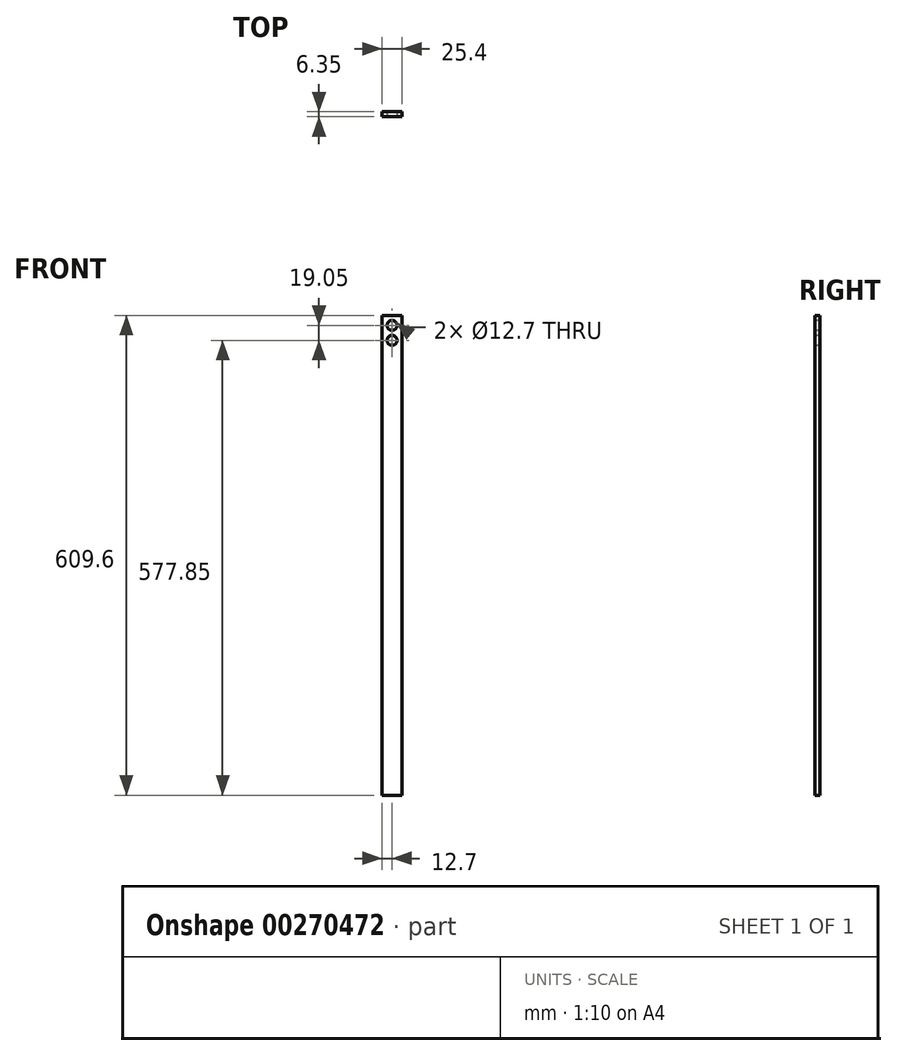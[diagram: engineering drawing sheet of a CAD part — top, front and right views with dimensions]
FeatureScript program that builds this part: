
annotation { "Feature Type Name" : "Feature", "Feature Type Description" : "" }
export const myFeature = defineFeature(function(context is Context, id is Id, definition is map)
    precondition{}
    {
        {
            var Q0;
            Q0=qCreatedBy(makeId("Front.planeOp"),FACE);
            var sketch = newSketch(context, id + "F0", { "sketchPlane" : qUnion([Q0])});
            skLineSegment(sketch, "E0.bottom", {"start": v(0, 0) * mm, "end": v(25.4, 0) * mm});
            skLineSegment(sketch, "E0.top", {"start": v(0, 609.6) * mm, "end": v(25.4, 609.6) * mm});
            skLineSegment(sketch, "E0.left", {"start": v(0, 0) * mm, "end": v(0, 609.6) * mm});
            skLineSegment(sketch, "E0.right", {"start": v(25.4, 0) * mm, "end": v(25.4, 609.6) * mm});
            skSolve(sketch);
        }
        {
            var Q0;
            Q0 = qSketchRegion(id + "F0", true);
            extrude(context, id + "F1", {"entities" : qUnion([Q0]), "depth" : 6.35 * mm});
        }
        {
            var Q0;
            Q0=makeQuery(id+"F1.opExtrude","CAP_FACE",FACE,{"disambiguationData":[OSD([sQuery(id+"F0.wireOp",EDGE,"E0.bottom"),sQuery(id+"F0.wireOp",EDGE,"E0.top"),sQuery(id+"F0.wireOp",EDGE,"E0.left"),sQuery(id+"F0.wireOp",EDGE,"E0.right")])],"isStart":false});
            var sketch = newSketch(context, id + "F2", { "sketchPlane" : qUnion([Q0])});
            skLineSegment(sketch, "E1", {"start": v(12.7, 0) * mm, "end": v(12.7, 609.6) * mm, "construction": true});
            skCircle(sketch, "E2", {"center": v(12.7, 596.9) * mm, "radius": 6.35 * mm});
            skCircle(sketch, "E3", {"center": v(12.7, 577.85) * mm, "radius": 6.35 * mm});
            skSolve(sketch);
        }
        {
            var Q0;
            Q0 = qSketchRegion(id + "F2", true);
            extrude(context, id + "F3", {"entities" : qUnion([Q0]), "operationType" : NewBodyOperationType.REMOVE, "endBound" : BoundingType.UP_TO_NEXT, "oppositeDirection" : true, "depth" : 25.4 * mm});
        }
    });
